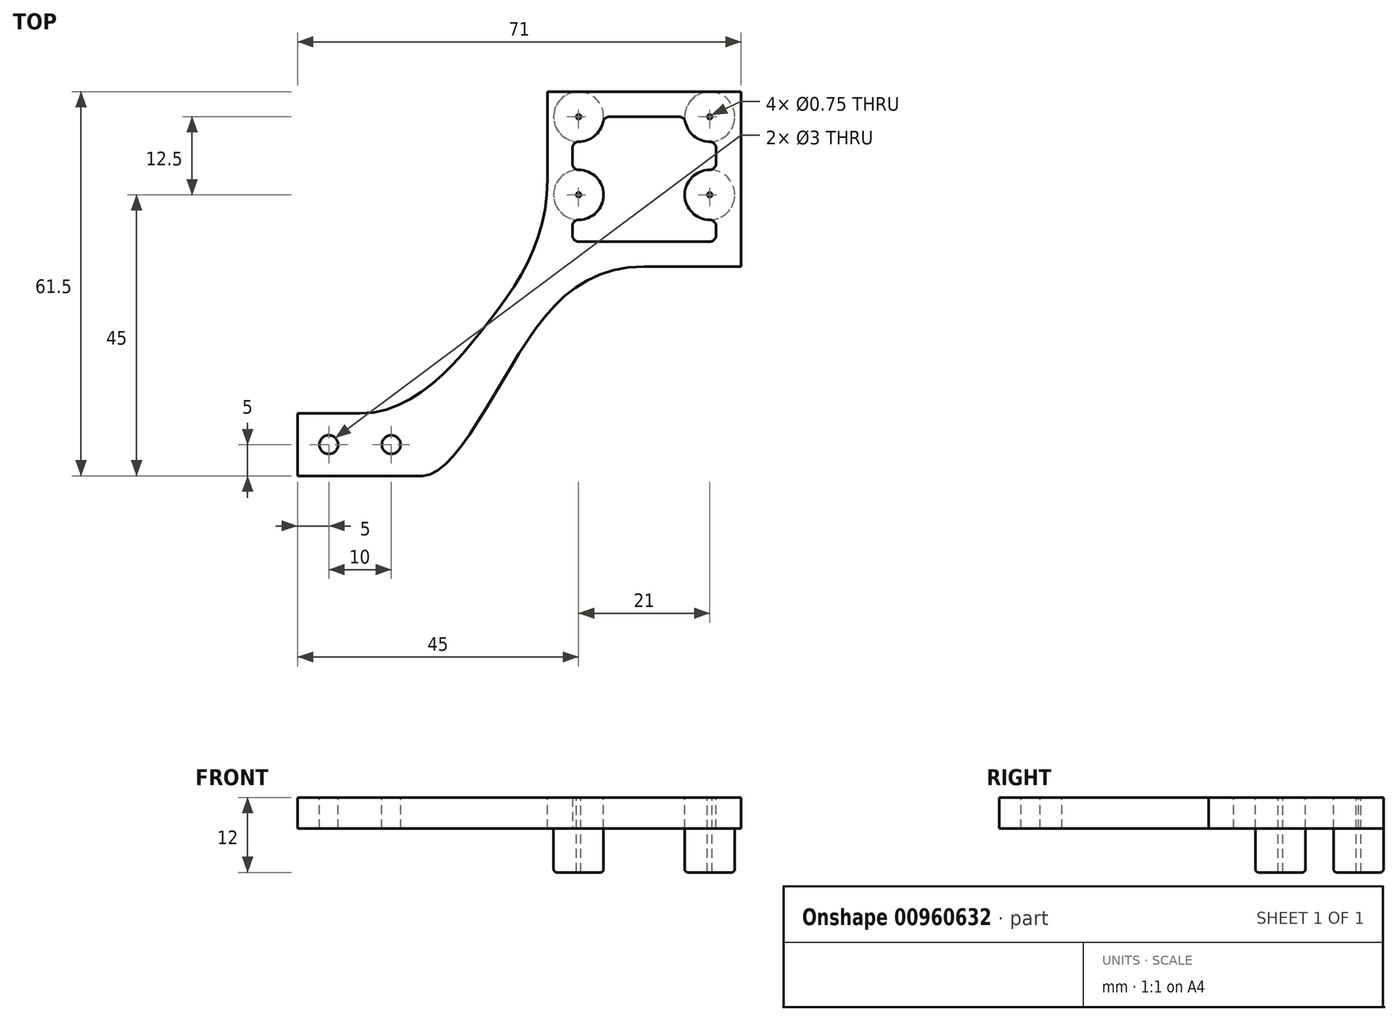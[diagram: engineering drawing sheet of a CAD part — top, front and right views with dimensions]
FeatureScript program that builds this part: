
annotation { "Feature Type Name" : "Feature", "Feature Type Description" : "" }
export const myFeature = defineFeature(function(context is Context, id is Id, definition is map)
    precondition{}
    {
        {
            var Q0;
            Q0=qCreatedBy(makeId("Top.planeOp"),FACE);
            var sketch = newSketch(context, id + "F0", { "sketchPlane" : qUnion([Q0])});
            skLineSegment(sketch, "E0.bottom", {"start": v(15.5, -14) * mm, "end": v(-15.5, -14) * mm});
            skLineSegment(sketch, "E0.top", {"start": v(15.5, 14) * mm, "end": v(-15.5, 14) * mm});
            skLineSegment(sketch, "E0.left", {"start": v(15.5, -14) * mm, "end": v(15.5, 14) * mm});
            skLineSegment(sketch, "E0.right", {"start": v(-15.5, -14) * mm, "end": v(-15.5, 14) * mm});
            skPoint(sketch, "E0.middle", {"position": v(0, 0) * mm});
            skLineSegment(sketch, "E1.bottom", {"start": v(11.5, -10) * mm, "end": v(-11.5, -10) * mm});
            skLineSegment(sketch, "E1.top", {"start": v(11.5, 10) * mm, "end": v(-11.5, 10) * mm});
            skLineSegment(sketch, "E1.left", {"start": v(11.5, -10) * mm, "end": v(11.5, 10) * mm});
            skLineSegment(sketch, "E1.right", {"start": v(-11.5, -10) * mm, "end": v(-11.5, 10) * mm});
            skCircle(sketch, "E2", {"center": v(-10.5, 10) * mm, "radius": 0.38 * mm});
            skCircle(sketch, "E3", {"center": v(10.5, 10) * mm, "radius": 0.37 * mm});
            skCircle(sketch, "E4", {"center": v(-10.5, -2.5) * mm, "radius": 0.38 * mm});
            skCircle(sketch, "E5", {"center": v(10.5, -2.5) * mm, "radius": 0.38 * mm});
            skCircle(sketch, "E6", {"center": v(-10.5, -2.5) * mm, "radius": 4 * mm});
            skCircle(sketch, "E7", {"center": v(10.5, -2.5) * mm, "radius": 4 * mm});
            skCircle(sketch, "E8", {"center": v(10.5, 10) * mm, "radius": 4 * mm});
            skCircle(sketch, "E9", {"center": v(-10.5, 10) * mm, "radius": 4 * mm});
            skCircle(sketch, "E10", {"center": v(-50.5, -42.5) * mm, "radius": 1.5 * mm});
            skCircle(sketch, "E11", {"center": v(-40.5, -42.5) * mm, "radius": 1.5 * mm});
            skLineSegment(sketch, "E12.bottom", {"start": v(-55.5, -37.5) * mm, "end": v(-35.5, -37.5) * mm});
            skLineSegment(sketch, "E12.top", {"start": v(-55.5, -47.5) * mm, "end": v(-35.5, -47.5) * mm});
            skLineSegment(sketch, "E12.left", {"start": v(-55.5, -37.5) * mm, "end": v(-55.5, -47.5) * mm});
            skLineSegment(sketch, "E12.right", {"start": v(-35.5, -37.5) * mm, "end": v(-35.5, -47.5) * mm});
            skFitSpline(sketch, "E13", {"points": [v(-15.5, 0) * mm, v(-25.78, -23.96) * mm, v(-45.5, -37.5) * mm], "startDerivative": vector(0, -58.72) * mm, "endDerivative": vector(-50.49, 0) * mm});
            skFitSpline(sketch, "E14", {"points": [v(-35.5, -47.5) * mm, v(-21.34, -30.03) * mm, v(0, -14) * mm], "startDerivative": vector(27.8, 0) * mm, "endDerivative": vector(61.84, 0) * mm});
            skSolve(sketch);
        }
        {
            var Q0;
            Q0=makeQuery(id+"F0.imprint","IMPRINT",FACE,{"disambiguationData":[TD([[makeQuery(id+"F0.imprint","IMPRINT",EDGE,{"derivedFrom":sQuery(id+"F0.wireOp",EDGE,"E0.bottom")}),-1.0]])]});
            var Q1;
            Q1=makeQuery(id+"F0.imprint","IMPRINT",FACE,{"disambiguationData":[TD([[makeQuery(id+"F0.imprint","IMPRINT",EDGE,{"derivedFrom":sQuery(id+"F0.wireOp",EDGE,"E5")}),-1.0]])]});
            var Q2;
            {var subQ1=sQuery(id+"F0.wireOp",EDGE,"E1.top");var subQ6=sQuery(id+"F0.wireOp",EDGE,"E1.left");var subQ7=makeQuery(id+"F0.imprint","INTERSECT",VERTEX,{"derivedFrom":[subQ1,subQ6]});Q2=makeQuery(id+"F0.imprint","IMPRINT",FACE,{"disambiguationData":[TD([[makeQuery(id+"F0.imprint","IMPRINT",EDGE,{"disambiguationData":[TD([[subQ7,-1.0]])],"derivedFrom":subQ1}),1.0]])]});}
            var Q3;
            {var subQ1=sQuery(id+"F0.wireOp",EDGE,"E1.top");var subQ6=sQuery(id+"F0.wireOp",EDGE,"E1.left");var subQ7=makeQuery(id+"F0.imprint","INTERSECT",VERTEX,{"derivedFrom":[subQ1,subQ6]});Q3=makeQuery(id+"F0.imprint","IMPRINT",FACE,{"disambiguationData":[TD([[makeQuery(id+"F0.imprint","IMPRINT",EDGE,{"disambiguationData":[TD([[subQ7,-1.0]])],"derivedFrom":subQ1}),-1.0]])]});}
            var Q4;
            {var subQ0=sQuery(id+"F0.wireOp",EDGE,"E7");var subQ1=sQuery(id+"F0.wireOp",EDGE,"E1.left");var subQ2=makeQuery(id+"F0.imprint","INTERSECT",VERTEX,{"disambiguationData":[OD(0.0)],"derivedFrom":[subQ1,subQ0]});Q4=makeQuery(id+"F0.imprint","IMPRINT",FACE,{"disambiguationData":[TD([[makeQuery(id+"F0.imprint","IMPRINT",EDGE,{"disambiguationData":[TD([[subQ2,-1.0]])],"derivedFrom":subQ1}),-1.0]])]});}
            var Q5;
            Q5=makeQuery(id+"F0.imprint","IMPRINT",FACE,{"disambiguationData":[TD([[makeQuery(id+"F0.imprint","IMPRINT",EDGE,{"derivedFrom":sQuery(id+"F0.wireOp",EDGE,"E4")}),-1.0]])]});
            var Q6;
            {var subQ0=sQuery(id+"F0.wireOp",EDGE,"E6");var subQ1=sQuery(id+"F0.wireOp",EDGE,"E1.right");var subQ2=makeQuery(id+"F0.imprint","INTERSECT",VERTEX,{"disambiguationData":[OD(0.0)],"derivedFrom":[subQ1,subQ0]});Q6=makeQuery(id+"F0.imprint","IMPRINT",FACE,{"disambiguationData":[TD([[makeQuery(id+"F0.imprint","IMPRINT",EDGE,{"disambiguationData":[TD([[subQ2,-1.0]])],"derivedFrom":subQ1}),1.0]])]});}
            var Q7;
            {var subQ1=sQuery(id+"F0.wireOp",EDGE,"E1.top");var subQ6=sQuery(id+"F0.wireOp",EDGE,"E9");var subQ8=makeQuery(id+"F0.imprint","INTERSECT",VERTEX,{"derivedFrom":[subQ1,subQ6]});Q7=makeQuery(id+"F0.imprint","IMPRINT",FACE,{"disambiguationData":[TD([[makeQuery(id+"F0.imprint","IMPRINT",EDGE,{"disambiguationData":[TD([[subQ8,-1.0]])],"derivedFrom":subQ1}),-1.0]])]});}
            var Q8;
            {var subQ0=sQuery(id+"F0.wireOp",EDGE,"E8");var subQ1=sQuery(id+"F0.wireOp",EDGE,"E0.top");var subQ2=makeQuery(id+"F0.imprint","INTERSECT",VERTEX,{"derivedFrom":[subQ1,subQ0]});Q8=makeQuery(id+"F0.imprint","IMPRINT",FACE,{"disambiguationData":[TD([[makeQuery(id+"F0.imprint","IMPRINT",EDGE,{"disambiguationData":[TD([[subQ2,-1.0]])],"derivedFrom":subQ1}),1.0]])]});}
            var Q9;
            {var subQ1=sQuery(id+"F0.wireOp",EDGE,"E1.top");var subQ4=sQuery(id+"F0.wireOp",EDGE,"E9");var subQ5=makeQuery(id+"F0.imprint","INTERSECT",VERTEX,{"derivedFrom":[subQ1,subQ4]});Q9=makeQuery(id+"F0.imprint","IMPRINT",FACE,{"disambiguationData":[TD([[makeQuery(id+"F0.imprint","IMPRINT",EDGE,{"disambiguationData":[TD([[subQ5,-1.0]])],"derivedFrom":subQ1}),1.0]])]});}
            var Q10;
            {var subQ0=sQuery(id+"F0.wireOp",EDGE,"E12.right");Q10=makeQuery(id+"F0.imprint","IMPRINT",FACE,{"disambiguationData":[TD([[makeQuery(id+"F0.imprint","IMPRINT",EDGE,{"derivedFrom":subQ0}),1.0]])]});}
            var Q11;
            Q11=makeQuery(id+"F0.imprint","IMPRINT",FACE,{"disambiguationData":[TD([[makeQuery(id+"F0.imprint","IMPRINT",EDGE,{"derivedFrom":sQuery(id+"F0.wireOp",EDGE,"E10")}),-1.0]])]});
            extrude(context, id + "F1", {"entities" : qUnion([Q0, Q1, Q2, Q3, Q4, Q5, Q6, Q7, Q8, Q9, Q10, Q11]), "depth" : -5 * mm, "offsetDistance" : 25 * mm});
        }
        {
            var Q0;
            Q0=makeQuery(id+"F0.imprint","IMPRINT",FACE,{"disambiguationData":[TD([[makeQuery(id+"F0.imprint","IMPRINT",EDGE,{"derivedFrom":sQuery(id+"F0.wireOp",EDGE,"E5")}),-1.0]])]});
            var Q1;
            {var subQ0=sQuery(id+"F0.wireOp",EDGE,"E7");var subQ1=sQuery(id+"F0.wireOp",EDGE,"E1.left");var subQ2=makeQuery(id+"F0.imprint","INTERSECT",VERTEX,{"disambiguationData":[OD(0.0)],"derivedFrom":[subQ1,subQ0]});Q1=makeQuery(id+"F0.imprint","IMPRINT",FACE,{"disambiguationData":[TD([[makeQuery(id+"F0.imprint","IMPRINT",EDGE,{"disambiguationData":[TD([[subQ2,-1.0]])],"derivedFrom":subQ1}),-1.0]])]});}
            var Q2;
            {var subQ1=sQuery(id+"F0.wireOp",EDGE,"E1.top");var subQ6=sQuery(id+"F0.wireOp",EDGE,"E1.left");var subQ7=makeQuery(id+"F0.imprint","INTERSECT",VERTEX,{"derivedFrom":[subQ1,subQ6]});Q2=makeQuery(id+"F0.imprint","IMPRINT",FACE,{"disambiguationData":[TD([[makeQuery(id+"F0.imprint","IMPRINT",EDGE,{"disambiguationData":[TD([[subQ7,-1.0]])],"derivedFrom":subQ1}),1.0]])]});}
            var Q3;
            {var subQ1=sQuery(id+"F0.wireOp",EDGE,"E1.top");var subQ6=sQuery(id+"F0.wireOp",EDGE,"E1.left");var subQ7=makeQuery(id+"F0.imprint","INTERSECT",VERTEX,{"derivedFrom":[subQ1,subQ6]});Q3=makeQuery(id+"F0.imprint","IMPRINT",FACE,{"disambiguationData":[TD([[makeQuery(id+"F0.imprint","IMPRINT",EDGE,{"disambiguationData":[TD([[subQ7,-1.0]])],"derivedFrom":subQ1}),-1.0]])]});}
            var Q4;
            Q4=makeQuery(id+"F0.imprint","IMPRINT",FACE,{"disambiguationData":[TD([[makeQuery(id+"F0.imprint","IMPRINT",EDGE,{"derivedFrom":sQuery(id+"F0.wireOp",EDGE,"E4")}),-1.0]])]});
            var Q5;
            {var subQ0=sQuery(id+"F0.wireOp",EDGE,"E6");var subQ1=sQuery(id+"F0.wireOp",EDGE,"E1.right");var subQ2=makeQuery(id+"F0.imprint","INTERSECT",VERTEX,{"disambiguationData":[OD(0.0)],"derivedFrom":[subQ1,subQ0]});Q5=makeQuery(id+"F0.imprint","IMPRINT",FACE,{"disambiguationData":[TD([[makeQuery(id+"F0.imprint","IMPRINT",EDGE,{"disambiguationData":[TD([[subQ2,-1.0]])],"derivedFrom":subQ1}),1.0]])]});}
            var Q6;
            {var subQ1=sQuery(id+"F0.wireOp",EDGE,"E1.top");var subQ6=sQuery(id+"F0.wireOp",EDGE,"E9");var subQ8=makeQuery(id+"F0.imprint","INTERSECT",VERTEX,{"derivedFrom":[subQ1,subQ6]});Q6=makeQuery(id+"F0.imprint","IMPRINT",FACE,{"disambiguationData":[TD([[makeQuery(id+"F0.imprint","IMPRINT",EDGE,{"disambiguationData":[TD([[subQ8,-1.0]])],"derivedFrom":subQ1}),-1.0]])]});}
            var Q7;
            {var subQ1=sQuery(id+"F0.wireOp",EDGE,"E1.top");var subQ4=sQuery(id+"F0.wireOp",EDGE,"E9");var subQ5=makeQuery(id+"F0.imprint","INTERSECT",VERTEX,{"derivedFrom":[subQ1,subQ4]});Q7=makeQuery(id+"F0.imprint","IMPRINT",FACE,{"disambiguationData":[TD([[makeQuery(id+"F0.imprint","IMPRINT",EDGE,{"disambiguationData":[TD([[subQ5,-1.0]])],"derivedFrom":subQ1}),1.0]])]});}
            extrude(context, id + "F2", {"entities" : qUnion([Q0, Q1, Q2, Q3, Q4, Q5, Q6, Q7]), "operationType" : NewBodyOperationType.ADD, "oppositeDirection" : true, "depth" : 12 * mm, "offsetDistance" : 25 * mm, "hasSecondDirection" : true, "secondDirectionOppositeDirection" : true, "secondDirectionDepth" : 5 * mm});
        }
        {
            var Q0;
            {var subQ0=sQuery(id+"F0.wireOp",EDGE,"E6");var subQ1=sQuery(id+"F0.wireOp",EDGE,"E1.right");Q0=makeQuery(id+"F1.opExtrude","SWEPT_EDGE",EDGE,{"disambiguationData":[OSD([subQ1,subQ0]),TDD([makeQuery(id+"F0.imprint","INTERSECT",VERTEX,{"disambiguationData":[OD(0.0)],"derivedFrom":[subQ1,subQ0]})])]});}
            var Q1;
            {var subQ0=sQuery(id+"F0.wireOp",EDGE,"E7");var subQ1=sQuery(id+"F0.wireOp",EDGE,"E1.left");Q1=makeQuery(id+"F1.opExtrude","SWEPT_EDGE",EDGE,{"disambiguationData":[OSD([subQ1,subQ0]),TDD([makeQuery(id+"F0.imprint","INTERSECT",VERTEX,{"disambiguationData":[OD(0.0)],"derivedFrom":[subQ1,subQ0]})])]});}
            var Q2;
            Q2=makeQuery(id+"F1.opExtrude","SWEPT_EDGE",EDGE,{"disambiguationData":[OSD([sQuery(id+"F0.wireOp",EDGE,"E1.left"),sQuery(id+"F0.wireOp",EDGE,"E8")])]});
            var Q3;
            Q3=makeQuery(id+"F1.opExtrude","SWEPT_EDGE",EDGE,{"disambiguationData":[OSD([sQuery(id+"F0.wireOp",EDGE,"E1.top"),sQuery(id+"F0.wireOp",EDGE,"E8")])]});
            var Q4;
            Q4=makeQuery(id+"F1.opExtrude","SWEPT_EDGE",EDGE,{"disambiguationData":[OSD([sQuery(id+"F0.wireOp",EDGE,"E1.top"),sQuery(id+"F0.wireOp",EDGE,"E9")])]});
            var Q5;
            Q5=makeQuery(id+"F1.opExtrude","SWEPT_EDGE",EDGE,{"disambiguationData":[OSD([sQuery(id+"F0.wireOp",EDGE,"E1.right"),sQuery(id+"F0.wireOp",EDGE,"E9")])]});
            var Q6;
            {var subQ0=sQuery(id+"F0.wireOp",EDGE,"E6");var subQ1=sQuery(id+"F0.wireOp",EDGE,"E1.right");Q6=makeQuery(id+"F1.opExtrude","SWEPT_EDGE",EDGE,{"disambiguationData":[OSD([subQ1,subQ0]),TDD([makeQuery(id+"F0.imprint","INTERSECT",VERTEX,{"disambiguationData":[OD(1.0)],"derivedFrom":[subQ1,subQ0]})])]});}
            var Q7;
            {var subQ0=sQuery(id+"F0.wireOp",EDGE,"E7");var subQ1=sQuery(id+"F0.wireOp",EDGE,"E1.left");Q7=makeQuery(id+"F1.opExtrude","SWEPT_EDGE",EDGE,{"disambiguationData":[OSD([subQ1,subQ0]),TDD([makeQuery(id+"F0.imprint","INTERSECT",VERTEX,{"disambiguationData":[OD(1.0)],"derivedFrom":[subQ1,subQ0]})])]});}
            var Q8;
            Q8=makeQuery(id+"F1.opExtrude","SWEPT_EDGE",EDGE,{"disambiguationData":[OSD([sQuery(id+"F0.wireOp",EDGE,"E1.bottom"),sQuery(id+"F0.wireOp",EDGE,"E1.left")])]});
            var Q9;
            Q9=makeQuery(id+"F1.opExtrude","SWEPT_EDGE",EDGE,{"disambiguationData":[OSD([sQuery(id+"F0.wireOp",EDGE,"E1.bottom"),sQuery(id+"F0.wireOp",EDGE,"E1.right")])]});
            fillet(context, id + "F3", {"entities" : qUnion([Q0, Q1, Q2, Q3, Q4, Q5, Q6, Q7, Q8, Q9]), "radius" : 1 * mm, "tangentPropagation" : true, "allowEdgeOverflow" : false});
        }
        {
            var Q0;
            Q0=makeQuery(id+"F2.opExtrude","CAP_EDGE",EDGE,{"disambiguationData":[OSD([sQuery(id+"F0.wireOp",EDGE,"E6")])],"isStart":false});
            var Q1;
            Q1=makeQuery(id+"F2.opExtrude","CAP_EDGE",EDGE,{"disambiguationData":[OSD([sQuery(id+"F0.wireOp",EDGE,"E7")])],"isStart":false});
            var Q2;
            Q2=makeQuery(id+"F2.opExtrude","CAP_EDGE",EDGE,{"disambiguationData":[OSD([sQuery(id+"F0.wireOp",EDGE,"E9")])],"isStart":false});
            var Q3;
            Q3=makeQuery(id+"F2.opExtrude","CAP_EDGE",EDGE,{"disambiguationData":[OSD([sQuery(id+"F0.wireOp",EDGE,"E8")])],"isStart":false});
            fillet(context, id + "F4", {"entities" : qUnion([Q0, Q1, Q2, Q3]), "radius" : 0.5 * mm, "tangentPropagation" : true, "allowEdgeOverflow" : false});
        }
    });
